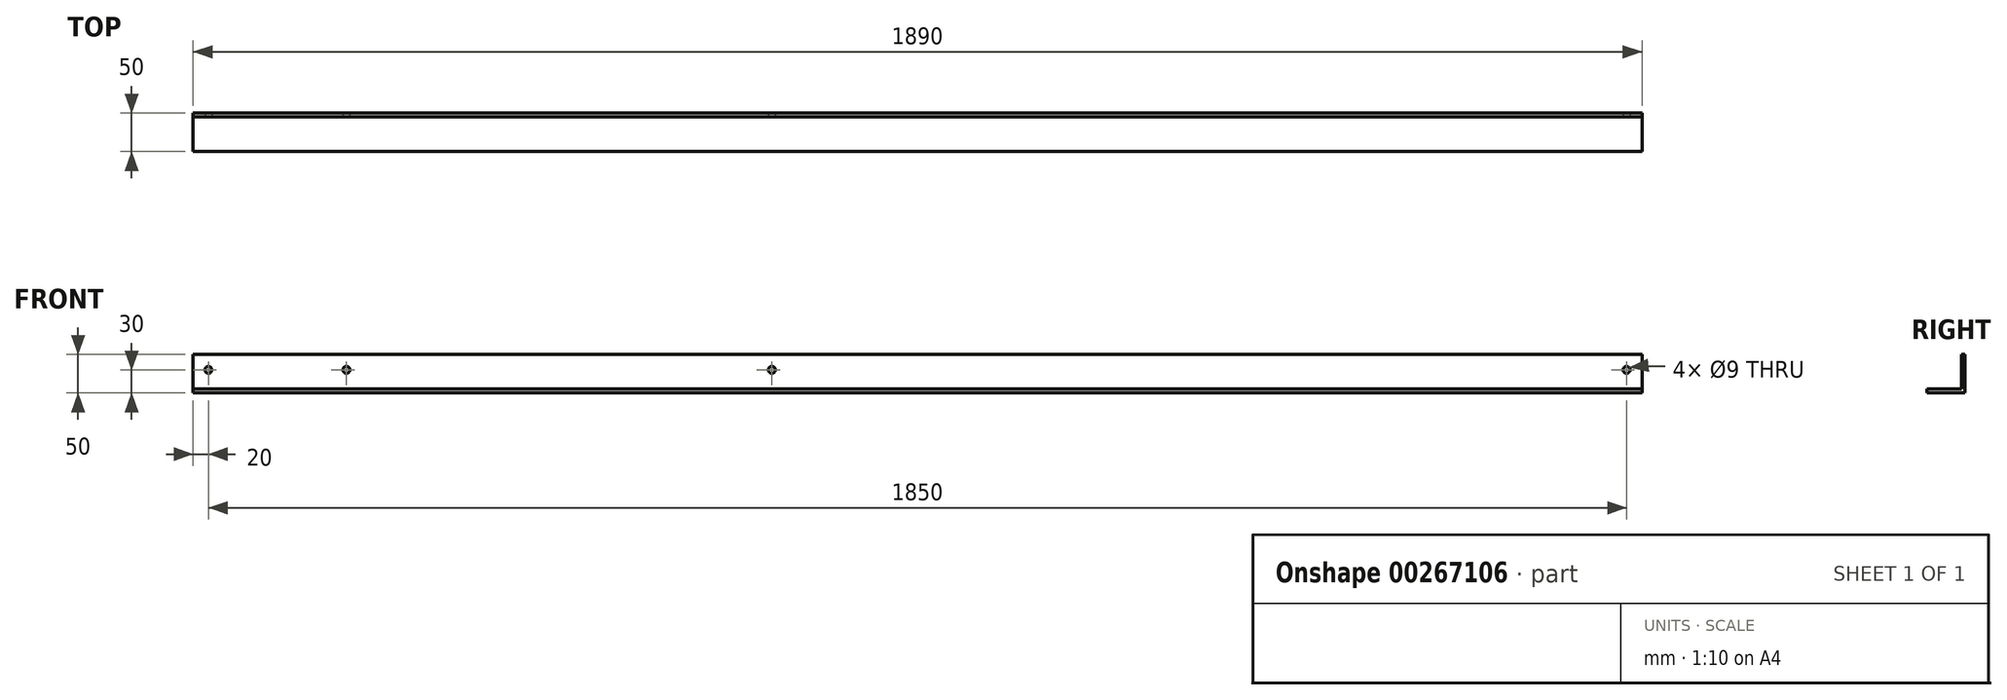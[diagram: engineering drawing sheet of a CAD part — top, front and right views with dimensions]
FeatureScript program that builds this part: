
annotation { "Feature Type Name" : "Feature", "Feature Type Description" : "" }
export const myFeature = defineFeature(function(context is Context, id is Id, definition is map)
    precondition{}
    {
        {
            var Q0;
            Q0=qCreatedBy(makeId("Right.planeOp"),FACE);
            var sketch = newSketch(context, id + "F0", { "sketchPlane" : qUnion([Q0])});
            skLineSegment(sketch, "E0.bottom", {"start": v(-50, 5) * mm, "end": v(0, 5) * mm});
            skLineSegment(sketch, "E0.top", {"start": v(-50, 0) * mm, "end": v(0, 0) * mm});
            skLineSegment(sketch, "E0.left", {"start": v(-50, 5) * mm, "end": v(-50, 0) * mm});
            skLineSegment(sketch, "E0.right", {"start": v(0, 5) * mm, "end": v(0, 0) * mm});
            skLineSegment(sketch, "E1.bottom", {"start": v(0, 0) * mm, "end": v(-5, 0) * mm});
            skLineSegment(sketch, "E1.top", {"start": v(0, 50) * mm, "end": v(-5, 50) * mm});
            skLineSegment(sketch, "E1.left", {"start": v(0, 0) * mm, "end": v(0, 50) * mm});
            skLineSegment(sketch, "E1.right", {"start": v(-5, 0) * mm, "end": v(-5, 50) * mm});
            skSolve(sketch);
        }
        {
            var Q0;
            {var subQ4=sQuery(id+"F0.wireOp",EDGE,"E0.top");Q0=makeQuery(id+"F0.imprint","IMPRINT",FACE,{"disambiguationData":[TD([[makeQuery(id+"F0.imprint","IMPRINT",EDGE,{"derivedFrom":subQ4}),1.0]])]});}
            var Q1;
            {var subQ5=sQuery(id+"F0.wireOp",EDGE,"E1.bottom");Q1=makeQuery(id+"F0.imprint","IMPRINT",FACE,{"disambiguationData":[TD([[makeQuery(id+"F0.imprint","IMPRINT",EDGE,{"derivedFrom":subQ5}),-1.0]])]});}
            var Q2;
            {var subQ5=sQuery(id+"F0.wireOp",EDGE,"E1.top");Q2=makeQuery(id+"F0.imprint","IMPRINT",FACE,{"disambiguationData":[TD([[makeQuery(id+"F0.imprint","IMPRINT",EDGE,{"derivedFrom":subQ5}),1.0]])]});}
            extrude(context, id + "F1", {"entities" : qUnion([Q0, Q1, Q2]), "endBound" : BoundingType.SYMMETRIC, "depth" : 1890 * mm});
        }
        {
            var Q0;
            Q0=makeQuery(id+"F1.opExtrude","SWEPT_FACE",FACE,{"disambiguationData":[OSD([sQuery(id+"F0.wireOp",EDGE,"E1.right")])]});
            var sketch = newSketch(context, id + "F2", { "sketchPlane" : qUnion([Q0])});
            skPoint(sketch, "E2", {"position": v(-925, 30) * mm});
            skPoint(sketch, "E3", {"position": v(925, 30) * mm});
            skPoint(sketch, "E4", {"position": v(-745, 30) * mm});
            skPoint(sketch, "E5", {"position": v(-190, 30) * mm});
            skSolve(sketch);
        }
        {
            var Q0;
            Q0 = qSketchRegion(id + "F2", true);
            var Q1;
            {var subQ0=sQuery(id+"F0.wireOp",EDGE,"E1.right");Q1=makeQuery(id+"F2.imprint","IMPRINT",FACE,{"disambiguationData":[TD([[makeQuery(id+"F2.imprint","IMPRINT",EDGE,{"derivedFrom":makeQuery(id+"F1.opExtrude","CAP_EDGE",EDGE,{"disambiguationData":[OSD([subQ0])],"isStart":true})}),-1.0]])]});}
            extrude(context, id + "F3", {"entities" : qUnion([Q0, Q1]), "operationType" : NewBodyOperationType.ADD, "oppositeDirection" : true, "depth" : 5 * mm});
        }
        {
            var Q0;
            Q0=sQuery(id+"F2.wireOp",VERTEX,"E2");
            var Q1;
            Q1=sQuery(id+"F2.wireOp",VERTEX,"E4");
            var Q2;
            Q2=sQuery(id+"F2.wireOp",VERTEX,"E5");
            var Q3;
            Q3=sQuery(id+"F2.wireOp",VERTEX,"E3");
            var Q4;
            Q4=makeQuery(id+"F1.opExtrude","SWEPT_BODY",BODY,{"disambiguationData":[OSD([sQuery(id+"F0.wireOp",EDGE,"E0.bottom"),sQuery(id+"F0.wireOp",EDGE,"E0.top"),sQuery(id+"F0.wireOp",EDGE,"E0.left"),sQuery(id+"F0.wireOp",EDGE,"E1.bottom"),sQuery(id+"F0.wireOp",EDGE,"E1.top"),sQuery(id+"F0.wireOp",EDGE,"E1.left"),sQuery(id+"F0.wireOp",EDGE,"E1.right")])]});
            hole(context, id + "F4", {"style" : HoleStyle.SIMPLE, "endStyle" : HoleEndStyle.THROUGH, "holeDiameter" : 9 * mm, "tappedDepth" : 12 * mm, "tapClearance" : 3, "startFromSketch" : true, "locations" : qUnion([Q0, Q1, Q2, Q3]), "scope" : qUnion([Q4])});
        }
    });
